# Revit family: BirdControl_Wire_BirdBGone_2000
name_source: partatom
category: Specialty Equipment
revit_build: Autodesk Revit 2017 (Build: 20160303_1130(x64)
units: mm (PartAtom-declared; Revit-internal decimal feet)

## family parameters
Cut with Voids When Loaded = No
OmniClass Number = 23.40.10.14.14.99
OmniClass Title = Other Manufactured Exterior Specialties
Part Type = Normal
Room Calculation Point = No
Round Connector Dimension = Use Diameter
Shared = No

## types (1)
- Wire System
    Assembly Code = E1090900
    Building Codes = http://www.birdbgone.com
    Construction Details = http://www.arcat.com
    Description = Bird Control Equipment as Specified in 10 81 19
    Expected Lifespan (Years) = 0
    Green Building-LEED = http://www.arcat.com
    Installation-Fabrication = http://www.birdbgone.com
    Keynote = 10 81 19
    Maintenance Schedule (Months) = 0
    Manufacturer = Bird-B-Gone, Inc.
    Manufacturer Fax = 949-472-3116
    Manufacturer Website = http://www.birdbgone.com
    Material = Metal - Stainless Steel - Bird B Gone
    Model = As Specified in 10 81 19
    Product Data = http://www.arcat.com
    Product Properties = http://www.arcat.com
    Revision = R1_10-2010
    Sales Information = http://www.birdbgone.com
    Send Message = http://www.arcat.com
    Specification = http://www.arcat.com
    Test Data = http://www.birdbgone.com
    URL = http://www.birdbgone.com
    Warranty Duration (Years) = 0

## geometry (parser evidence)
native form markers: Blend x26, Sweep x6
no freeform markers — native parametric forms only
